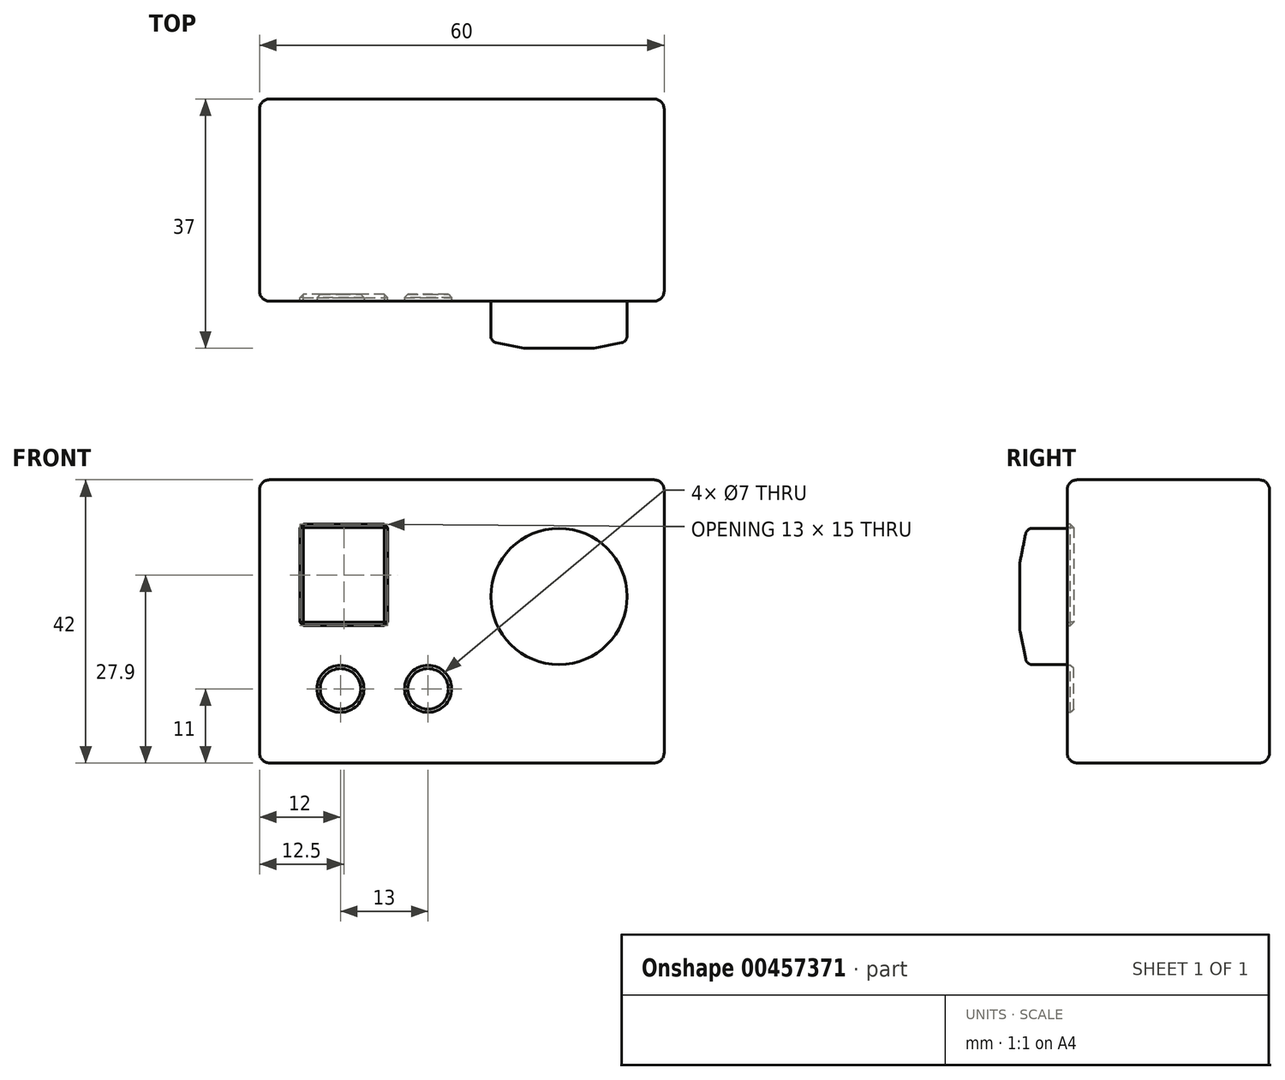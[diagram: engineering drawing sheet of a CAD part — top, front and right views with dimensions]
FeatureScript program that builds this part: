
annotation { "Feature Type Name" : "Feature", "Feature Type Description" : "" }
export const myFeature = defineFeature(function(context is Context, id is Id, definition is map)
    precondition{}
    {
        {
            var Q0;
            Q0=qCreatedBy(makeId("Front.planeOp"),FACE);
            var sketch = newSketch(context, id + "F0", { "sketchPlane" : qUnion([Q0])});
            skLineSegment(sketch, "E0.bottom", {"start": v(30, 21) * mm, "end": v(-30, 21) * mm});
            skLineSegment(sketch, "E0.top", {"start": v(30, -21) * mm, "end": v(-30, -21) * mm});
            skLineSegment(sketch, "E0.left", {"start": v(30, 21) * mm, "end": v(30, -21) * mm});
            skLineSegment(sketch, "E0.right", {"start": v(-30, 21) * mm, "end": v(-30, -21) * mm});
            skPoint(sketch, "E0.middle", {"position": v(0, 0) * mm});
            skSolve(sketch);
        }
        {
            var Q0;
            Q0=qSketchRegion(id+"F0",true);
            extrude(context, id + "F1", {"entities" : qUnion([Q0]), "depth" : 30 * mm});
        }
        {
            var Q0;
            Q0=makeQuery(id+"F1.opExtrude","CAP_FACE",FACE,{"disambiguationData":[OSD([sQuery(id+"F0.wireOp",EDGE,"E0.bottom"),sQuery(id+"F0.wireOp",EDGE,"E0.top"),sQuery(id+"F0.wireOp",EDGE,"E0.left"),sQuery(id+"F0.wireOp",EDGE,"E0.right")])],"isStart":false});
            var sketch = newSketch(context, id + "F2", { "sketchPlane" : qUnion([Q0])});
            skCircle(sketch, "E1", {"center": v(-18, -10) * mm, "radius": 3.5 * mm});
            skCircle(sketch, "E2", {"center": v(-5, -10) * mm, "radius": 3.5 * mm});
            skLineSegment(sketch, "E3.bottom", {"start": v(-24, 14.4) * mm, "end": v(-11, 14.4) * mm});
            skLineSegment(sketch, "E3.top", {"start": v(-24, -0.6) * mm, "end": v(-11, -0.6) * mm});
            skLineSegment(sketch, "E3.left", {"start": v(-24, 14.4) * mm, "end": v(-24, -0.6) * mm});
            skLineSegment(sketch, "E3.right", {"start": v(-11, 14.4) * mm, "end": v(-11, -0.6) * mm});
            skSolve(sketch);
        }
        {
            var Q0;
            Q0=qSketchRegion(id+"F2",true);
            extrude(context, id + "F3", {"entities" : qUnion([Q0]), "operationType" : NewBodyOperationType.REMOVE, "oppositeDirection" : true, "depth" : 1 * mm});
        }
        {
            var Q0;
            Q0=makeQuery(id+"F3.boolean.opBoolean","COPY",EDGE,{"derivedFrom":makeQuery(id+"F3.opExtrude","CAP_EDGE",EDGE,{"disambiguationData":[OSD([sQuery(id+"F2.wireOp",EDGE,"E1")])],"isStart":true})});
            var Q1;
            Q1=makeQuery(id+"F3.boolean.opBoolean","COPY",EDGE,{"derivedFrom":makeQuery(id+"F3.opExtrude","CAP_EDGE",EDGE,{"disambiguationData":[OSD([sQuery(id+"F2.wireOp",EDGE,"E2")])],"isStart":true})});
            var Q2;
            Q2=makeQuery(id+"F3.boolean.opBoolean","COPY",EDGE,{"derivedFrom":makeQuery(id+"F3.opExtrude","CAP_EDGE",EDGE,{"disambiguationData":[OSD([sQuery(id+"F2.wireOp",EDGE,"E3.right")])],"isStart":true})});
            var Q3;
            Q3=makeQuery(id+"F3.boolean.opBoolean","COPY",EDGE,{"derivedFrom":makeQuery(id+"F3.opExtrude","CAP_EDGE",EDGE,{"disambiguationData":[OSD([sQuery(id+"F2.wireOp",EDGE,"E1")])],"isStart":false})});
            var Q4;
            Q4=makeQuery(id+"F3.boolean.opBoolean","COPY",EDGE,{"derivedFrom":makeQuery(id+"F3.opExtrude","CAP_EDGE",EDGE,{"disambiguationData":[OSD([sQuery(id+"F2.wireOp",EDGE,"E2")])],"isStart":false})});
            var Q5;
            Q5=makeQuery(id+"F3.boolean.opBoolean","COPY",EDGE,{"derivedFrom":makeQuery(id+"F3.opExtrude","CAP_EDGE",EDGE,{"disambiguationData":[OSD([sQuery(id+"F2.wireOp",EDGE,"E3.bottom")])],"isStart":true})});
            var Q6;
            Q6=makeQuery(id+"F3.boolean.opBoolean","COPY",EDGE,{"derivedFrom":makeQuery(id+"F3.opExtrude","CAP_EDGE",EDGE,{"disambiguationData":[OSD([sQuery(id+"F2.wireOp",EDGE,"E3.top")])],"isStart":true})});
            var Q7;
            Q7=makeQuery(id+"F3.boolean.opBoolean","COPY",EDGE,{"derivedFrom":makeQuery(id+"F3.opExtrude","CAP_EDGE",EDGE,{"disambiguationData":[OSD([sQuery(id+"F2.wireOp",EDGE,"E3.left")])],"isStart":true})});
            var Q8;
            Q8=makeQuery(id+"F3.boolean.opBoolean","COPY",EDGE,{"derivedFrom":makeQuery(id+"F3.opExtrude","CAP_EDGE",EDGE,{"disambiguationData":[OSD([sQuery(id+"F2.wireOp",EDGE,"E3.left")])],"isStart":false})});
            var Q9;
            Q9=makeQuery(id+"F3.boolean.opBoolean","COPY",EDGE,{"derivedFrom":makeQuery(id+"F3.opExtrude","CAP_EDGE",EDGE,{"disambiguationData":[OSD([sQuery(id+"F2.wireOp",EDGE,"E3.right")])],"isStart":false})});
            var Q10;
            Q10=makeQuery(id+"F3.boolean.opBoolean","COPY",EDGE,{"derivedFrom":makeQuery(id+"F3.opExtrude","SWEPT_EDGE",EDGE,{"disambiguationData":[OSD([sQuery(id+"F2.wireOp",EDGE,"E3.bottom"),sQuery(id+"F2.wireOp",EDGE,"E3.left")])]})});
            var Q11;
            Q11=makeQuery(id+"F3.boolean.opBoolean","COPY",EDGE,{"derivedFrom":makeQuery(id+"F3.opExtrude","SWEPT_EDGE",EDGE,{"disambiguationData":[OSD([sQuery(id+"F2.wireOp",EDGE,"E3.bottom"),sQuery(id+"F2.wireOp",EDGE,"E3.right")])]})});
            var Q12;
            Q12=makeQuery(id+"F3.boolean.opBoolean","COPY",EDGE,{"derivedFrom":makeQuery(id+"F3.opExtrude","SWEPT_EDGE",EDGE,{"disambiguationData":[OSD([sQuery(id+"F2.wireOp",EDGE,"E3.top"),sQuery(id+"F2.wireOp",EDGE,"E3.left")])]})});
            var Q13;
            Q13=makeQuery(id+"F3.boolean.opBoolean","COPY",EDGE,{"derivedFrom":makeQuery(id+"F3.opExtrude","SWEPT_EDGE",EDGE,{"disambiguationData":[OSD([sQuery(id+"F2.wireOp",EDGE,"E3.top"),sQuery(id+"F2.wireOp",EDGE,"E3.right")])]})});
            var Q14;
            Q14=makeQuery(id+"F3.boolean.opBoolean","COPY",EDGE,{"derivedFrom":makeQuery(id+"F3.opExtrude","CAP_EDGE",EDGE,{"disambiguationData":[OSD([sQuery(id+"F2.wireOp",EDGE,"E3.bottom")])],"isStart":false})});
            var Q15;
            Q15=makeQuery(id+"F3.boolean.opBoolean","COPY",EDGE,{"derivedFrom":makeQuery(id+"F3.opExtrude","CAP_EDGE",EDGE,{"disambiguationData":[OSD([sQuery(id+"F2.wireOp",EDGE,"E3.top")])],"isStart":false})});
            chamfer(context, id + "F4", {"entities" : qUnion([Q0, Q1, Q2, Q3, Q4, Q5, Q6, Q7, Q8, Q9, Q10, Q11, Q12, Q13, Q14, Q15]), "width" : .5 * mm, "tangentPropagation" : true});
        }
        {
            var Q0;
            Q0=makeQuery(id+"F1.opExtrude","CAP_FACE",FACE,{"disambiguationData":[OSD([sQuery(id+"F0.wireOp",EDGE,"E0.bottom"),sQuery(id+"F0.wireOp",EDGE,"E0.top"),sQuery(id+"F0.wireOp",EDGE,"E0.left"),sQuery(id+"F0.wireOp",EDGE,"E0.right")])],"isStart":false});
            var sketch = newSketch(context, id + "F5", { "sketchPlane" : qUnion([Q0])});
            skCircle(sketch, "E4", {"center": v(14.4, 3.7) * mm, "radius": 10.1 * mm});
            skSolve(sketch);
        }
        {
            var Q0;
            Q0=qSketchRegion(id+"F5",true);
            extrude(context, id + "F6", {"entities" : qUnion([Q0]), "operationType" : NewBodyOperationType.ADD, "depth" : 7 * mm});
        }
        {
            var Q0;
            Q0=makeQuery(id+"F6.opExtrude","CAP_EDGE",EDGE,{"disambiguationData":[OSD([sQuery(id+"F5.wireOp",EDGE,"E4")])],"isStart":false});
            chamfer(context, id + "F7", {"entities" : qUnion([Q0]), "chamferType" : ChamferType.TWO_OFFSETS, "width1" : 5 * mm, "oppositeDirection" : false, "width2" : 1 * mm, "tangentPropagation" : true});
        }
        {
            var Q0;
            {var subQ0=sQuery(id+"F5.wireOp",EDGE,"E4");Q0=makeQuery(id+"F7.opChamfer","BLEND_EDGE",EDGE,{"blendedFrom":[makeQuery(id+"F6.opExtrude","CAP_EDGE",EDGE,{"disambiguationData":[OSD([subQ0])],"isStart":false}),makeQuery(id+"F6.opExtrude","CAP_FACE",FACE,{"disambiguationData":[OSD([subQ0])],"isStart":false})],"blendedInto":[makeQuery(id+"F6.opExtrude","CAP_FACE",FACE,{"disambiguationData":[OSD([subQ0])],"isStart":false})]});}
            var Q1;
            {var subQ0=sQuery(id+"F5.wireOp",EDGE,"E4");Q1=makeQuery(id+"F7.opChamfer","BLEND_EDGE",EDGE,{"blendedFrom":[makeQuery(id+"F6.opExtrude","CAP_EDGE",EDGE,{"disambiguationData":[OSD([subQ0])],"isStart":false}),makeQuery(id+"F6.opExtrude","SWEPT_FACE",FACE,{"disambiguationData":[OSD([subQ0])]})],"blendedInto":[makeQuery(id+"F6.opExtrude","SWEPT_FACE",FACE,{"disambiguationData":[OSD([subQ0])]})]});}
            fillet(context, id + "F8", {"entities" : qUnion([Q0, Q1]), "radius" : 1 * mm, "tangentPropagation" : true, "allowEdgeOverflow" : false});
        }
        {
            var Q0;
            Q0=makeQuery(id+"F1.opExtrude","SWEPT_FACE",FACE,{"disambiguationData":[OSD([sQuery(id+"F0.wireOp",EDGE,"E0.bottom")])]});
            var Q1;
            Q1=makeQuery(id+"F1.opExtrude","SWEPT_FACE",FACE,{"disambiguationData":[OSD([sQuery(id+"F0.wireOp",EDGE,"E0.left")])]});
            var Q2;
            Q2=makeQuery(id+"F1.opExtrude","SWEPT_FACE",FACE,{"disambiguationData":[OSD([sQuery(id+"F0.wireOp",EDGE,"E0.top")])]});
            var Q3;
            Q3=makeQuery(id+"F1.opExtrude","SWEPT_FACE",FACE,{"disambiguationData":[OSD([sQuery(id+"F0.wireOp",EDGE,"E0.right")])]});
            fillet(context, id + "F9", {"entities" : qUnion([Q0, Q1, Q2, Q3]), "radius" : 1.5 * mm, "tangentPropagation" : true, "allowEdgeOverflow" : false});
        }
        {
            var Q0;
            Q0=makeQuery(id+"F1.opExtrude","SWEPT_BODY",BODY,{"disambiguationData":[OSD([sQuery(id+"F0.wireOp",EDGE,"E0.bottom"),sQuery(id+"F0.wireOp",EDGE,"E0.top"),sQuery(id+"F0.wireOp",EDGE,"E0.left"),sQuery(id+"F0.wireOp",EDGE,"E0.right")])]});
            transform(context, id + "F10", {"entities" : qUnion([Q0]), "transformType" : TransformType.TRANSLATION_3D, "dx" : 0 * mm, "dy" : 0 * mm, "dz" : 0 * mm, "makeCopy" : true});
        }
    });
